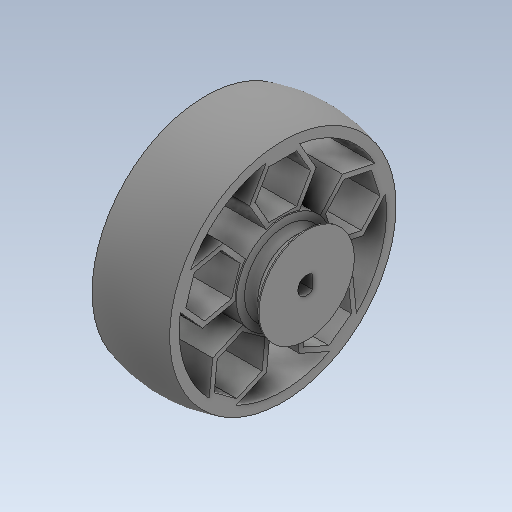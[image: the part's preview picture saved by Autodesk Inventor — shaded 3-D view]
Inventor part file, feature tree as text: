
AUTODESK INVENTOR PART (.ipt)
format: ipt  version: 2020 (Build 240168000, 168)  size: 415,744 bytes
history: native  units: in
note: dims shown in document units (in); Inventor stores cm internally (conversion verified against a paired STEP export)
features: sketch x4, extrude x2, revolve x2, projected_geometry x1
ambient origin geometry x8: Origin, YZ Plane, XZ Plane, XY Plane, X Axis, Y Axis, Z Axis, Center Point
bodies: Solid1 (feature_tree)
feature tree (9):
  extrude  "Extrusion1"  Depth=0.0394in
  sketch  "Sketch3"  dims[d6=0.6299in d7=0.1575in]
  revolve  "Revolution1"  [1 undecoded]
  extrude  "Extrusion2"  Depth=0.1575in
  revolve  "Revolution2"  [1 undecoded]
  sketch  "Sketch1"  dims[d0=0.1181in d1=0.0394in]
  sketch  "Sketch2"  dims[d3=1.4961in d4=0.1181in]
  projected_geometry  "Projected Loop1"
  sketch  "Sketch4"  dims[d8=0.0in d9=1.4961in d10=0.063in d11=0.0315in d16=0.5118in d17=0.0in d19=360.0deg d20=0.0787in d24=0.0394in d25=90.0deg d26=45.0deg d28=0.0079in d29=1.9685in d31=360.0deg]
note: 2 required parameter values undecoded (feature->parameter linkage not recoverable at this tier; creation-order binding heuristic only, values carry confidence <= 0.55)
